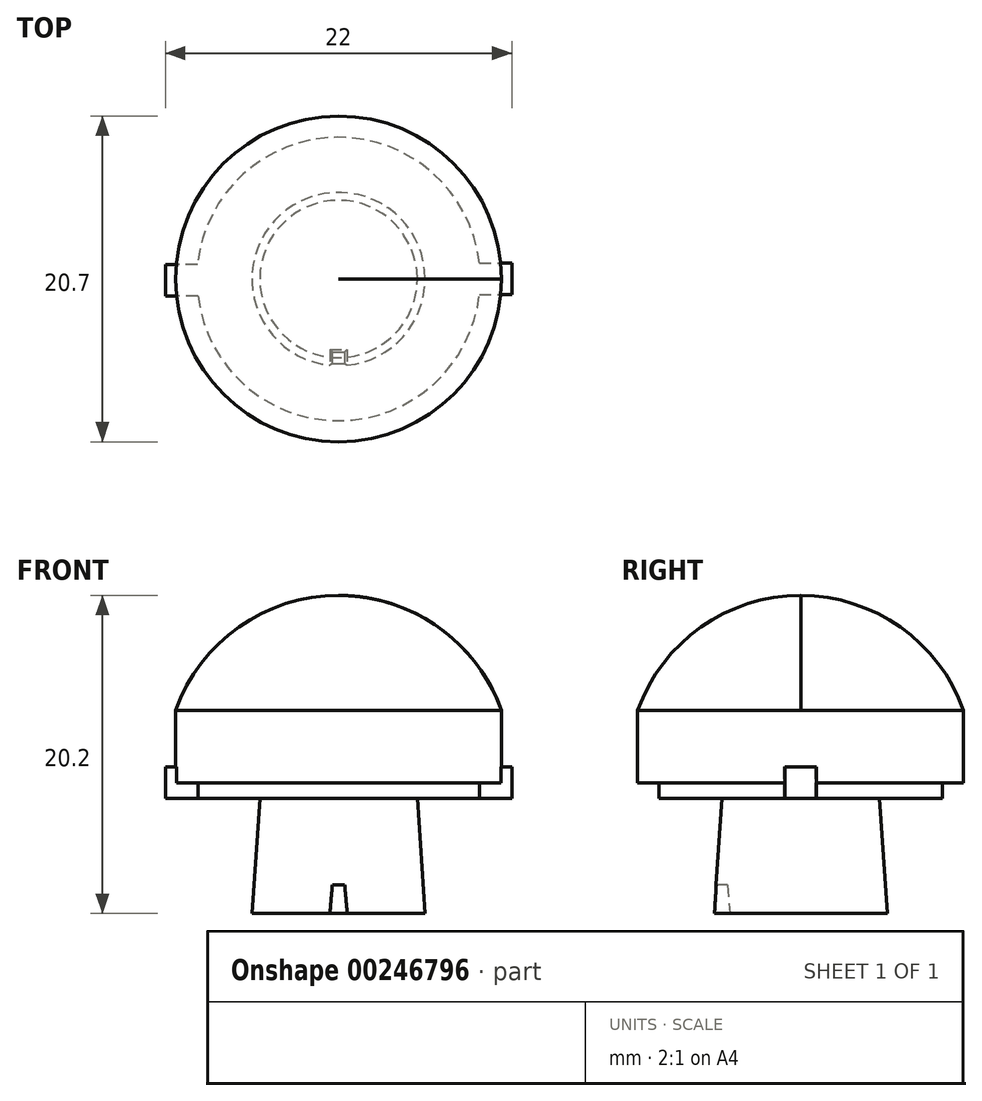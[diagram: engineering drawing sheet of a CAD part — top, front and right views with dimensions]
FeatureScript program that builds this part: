
annotation { "Feature Type Name" : "Feature", "Feature Type Description" : "" }
export const myFeature = defineFeature(function(context is Context, id is Id, definition is map)
    precondition{}
    {
        {
            var Q0;
            Q0=qCreatedBy(makeId("Front.planeOp"),FACE);
            var sketch = newSketch(context, id + "F0", { "sketchPlane" : qUnion([Q0])});
            skLineSegment(sketch, "E0", {"start": v(0, 0) * mm, "end": v(5.5, 0) * mm});
            skLineSegment(sketch, "E1", {"start": v(0, 20.2) * mm, "end": v(16.44, 20.2) * mm, "construction": true});
            skLineSegment(sketch, "E2", {"start": v(10.35, 7.3) * mm, "end": v(10.35, 0) * mm, "construction": true});
            skLineSegment(sketch, "E3", {"start": v(10.35, 7.3) * mm, "end": v(0, 7.3) * mm, "construction": true});
            skLineSegment(sketch, "E4", {"start": v(0, 7.3) * mm, "end": v(5, 7.3) * mm});
            skLineSegment(sketch, "E5", {"start": v(5, 7.3) * mm, "end": v(5.5, 0) * mm});
            skLineSegment(sketch, "E6", {"start": v(5, 7.3) * mm, "end": v(9, 7.3) * mm});
            skLineSegment(sketch, "E7", {"start": v(9, 7.3) * mm, "end": v(9, 8.3) * mm});
            skLineSegment(sketch, "E8", {"start": v(9, 7.3) * mm, "end": v(11, 7.3) * mm, "construction": true});
            skLineSegment(sketch, "E9", {"start": v(11, 7.3) * mm, "end": v(11, 9.3) * mm, "construction": true});
            skLineSegment(sketch, "E10", {"start": v(9, 8.3) * mm, "end": v(10.35, 8.3) * mm});
            skLineSegment(sketch, "E11", {"start": v(10.35, 8.3) * mm, "end": v(10.35, 9.3) * mm});
            skLineSegment(sketch, "E12", {"start": v(10.35, 9.3) * mm, "end": v(11, 9.3) * mm, "construction": true});
            skLineSegment(sketch, "E13", {"start": v(10.35, 9.3) * mm, "end": v(10.35, 12.9) * mm});
            skLineSegment(sketch, "E14", {"start": v(0, 12.9) * mm, "end": v(-10.35, 12.9) * mm, "construction": true});
            skLineSegment(sketch, "E15", {"start": v(0, 12.9) * mm, "end": v(10.35, 12.9) * mm, "construction": true});
            skArc(sketch, "E16", {"start": v(10.35, 12.9) * mm, "mid": v(6.33, 18.2) * mm, "end": v(0, 20.2) * mm});
            skLineSegment(sketch, "E17", {"start": v(0, 0) * mm, "end": v(0, 20.2) * mm});
            skSolve(sketch);
        }
        {
            var Q0;
            Q0=qSketchRegion(id+"F0",true);
            extrude(context, id + "F1", {"entities" : qUnion([Q0]), "depth" : 0.01 * mm});
        }
        {
            var Q0;
            Q0=makeQuery(id+"F1.opExtrude","CAP_FACE",FACE,{"disambiguationData":[OSD([sQuery(id+"F0.wireOp",EDGE,"E0"),sQuery(id+"F0.wireOp",EDGE,"E5"),sQuery(id+"F0.wireOp",EDGE,"E6"),sQuery(id+"F0.wireOp",EDGE,"E7"),sQuery(id+"F0.wireOp",EDGE,"E10"),sQuery(id+"F0.wireOp",EDGE,"E11"),sQuery(id+"F0.wireOp",EDGE,"E13"),sQuery(id+"F0.wireOp",EDGE,"E16"),sQuery(id+"F0.wireOp",EDGE,"74306cc8-111f-4a76-b4a3-b401b2c3296c0.MirrorCS"),sQuery(id+"F0.wireOp",EDGE,"74306cc8-111f-4a76-b4a3-b401b2c3296c2.MirrorCS"),sQuery(id+"F0.wireOp",EDGE,"74306cc8-111f-4a76-b4a3-b401b2c3296c3.MirrorCS"),sQuery(id+"F0.wireOp",EDGE,"74306cc8-111f-4a76-b4a3-b401b2c3296c6.MirrorCS"),sQuery(id+"F0.wireOp",EDGE,"74306cc8-111f-4a76-b4a3-b401b2c3296c7.MirrorCS"),sQuery(id+"F0.wireOp",EDGE,"74306cc8-111f-4a76-b4a3-b401b2c3296c9.MirrorCS"),sQuery(id+"F0.wireOp",EDGE,"74306cc8-111f-4a76-b4a3-b401b2c3296c13.MirrorCS")])],"isStart":false});
            var Q1;
            Q1=makeQuery(id+"F1.opExtrude","CAP_EDGE",EDGE,{"disambiguationData":[OSD([sQuery(id+"F0.wireOp",EDGE,"E17")])],"isStart":false});
            revolve(context, id + "F2", {"operationType" : NewBodyOperationType.ADD, "entities" : qUnion([Q0]), "axis" : qUnion([Q1]), "revolveType" : RevolveType.FULL});
        }
        {
            var Q0;
            {var subQ0=sQuery(id+"F0.wireOp",EDGE,"E0");Q0=makeQuery(id+"F2.boolean.opBoolean","MERGE",FACE,{"derivedFrom":[makeQuery(id+"F1.opExtrude","SWEPT_FACE",FACE,{"disambiguationData":[OSD([subQ0])]}),makeQuery(id+"F2.opRevolve","SWEPT_FACE",FACE,{"disambiguationData":[OSD([subQ0])]})]});}
            var sketch = newSketch(context, id + "F3", { "sketchPlane" : qUnion([Q0])});
            skCircle(sketch, "E18", {"center": v(0, 0) * mm, "radius": 6 * mm, "construction": true});
            skLineSegment(sketch, "E19", {"start": v(0, 6) * mm, "end": v(0, 4.5) * mm, "construction": true});
            skLineSegment(sketch, "E20", {"start": v(0, 4.5) * mm, "end": v(0.55, 4.5) * mm});
            skLineSegment(sketch, "E21", {"start": v(0.55, 4.5) * mm, "end": v(0.55, 5.97) * mm});
            skLineSegment(sketch, "E22", {"start": v(0, 4.5) * mm, "end": v(-0.55, 4.5) * mm});
            skLineSegment(sketch, "E23", {"start": v(-0.55, 4.5) * mm, "end": v(-0.55, 5.97) * mm});
            skLineSegment(sketch, "E24", {"start": v(-0.55, 5.97) * mm, "end": v(0.55, 5.97) * mm});
            skSolve(sketch);
        }
        {
            var Q0;
            Q0=qSketchRegion(id+"F3",true);
            extrude(context, id + "F4", {"entities" : qUnion([Q0]), "operationType" : NewBodyOperationType.REMOVE, "oppositeDirection" : true, "depth" : 1.8 * mm});
        }
        {
            var Q0;
            Q0=makeQuery(id+"F4.boolean.opBoolean","COPY",EDGE,{"derivedFrom":makeQuery(id+"F4.opExtrude","CAP_EDGE",EDGE,{"disambiguationData":[OSD([sQuery(id+"F3.wireOp",EDGE,"E23")])],"isStart":false})});
            var Q1;
            Q1=makeQuery(id+"F4.boolean.opBoolean","COPY",EDGE,{"derivedFrom":makeQuery(id+"F4.opExtrude","CAP_EDGE",EDGE,{"disambiguationData":[OSD([sQuery(id+"F3.wireOp",EDGE,"E21")])],"isStart":false})});
            var Q2;
            Q2=makeQuery(id+"F4.boolean.opBoolean","COPY",EDGE,{"derivedFrom":makeQuery(id+"F4.opExtrude","CAP_EDGE",EDGE,{"disambiguationData":[OSD([sQuery(id+"F3.wireOp",EDGE,"E20"),sQuery(id+"F3.wireOp",EDGE,"E22")])],"isStart":false})});
            chamfer(context, id + "F5", {"entities" : qUnion([Q0, Q1, Q2]), "chamferType" : ChamferType.OFFSET_ANGLE, "width" : 1.8 * mm, "oppositeDirection" : false, "angle" : 5 * degree, "tangentPropagation" : true});
        }
        {
            var Q0;
            Q0=qCreatedBy(makeId("Front.planeOp"),FACE);
            var sketch = newSketch(context, id + "F6", { "sketchPlane" : qUnion([Q0])});
            skLineSegment(sketch, "E25", {"start": v(10.35, 9.3) * mm, "end": v(11, 9.3) * mm});
            skLineSegment(sketch, "E26", {"start": v(11, 9.3) * mm, "end": v(11, 7.3) * mm});
            skLineSegment(sketch, "E27", {"start": v(11, 7.3) * mm, "end": v(9, 7.3) * mm});
            skLineSegment(sketch, "E28", {"start": v(9, 7.3) * mm, "end": v(9, 8.3) * mm});
            skLineSegment(sketch, "E29", {"start": v(9, 8.3) * mm, "end": v(10.35, 8.3) * mm});
            skLineSegment(sketch, "E30", {"start": v(10.35, 8.3) * mm, "end": v(10.35, 9.3) * mm});
            skLineSegment(sketch, "E31.MirrorCS", {"start": v(-10.35, 9.3) * mm, "end": v(-11, 9.3) * mm});
            skLineSegment(sketch, "E32.MirrorCS", {"start": v(-10.35, 8.3) * mm, "end": v(-10.35, 9.3) * mm});
            skLineSegment(sketch, "E33.MirrorCS", {"start": v(-9, 7.3) * mm, "end": v(-9, 8.3) * mm});
            skLineSegment(sketch, "E34.MirrorCS", {"start": v(-11, 7.3) * mm, "end": v(-9, 7.3) * mm});
            skLineSegment(sketch, "E35.MirrorCS", {"start": v(-11, 9.3) * mm, "end": v(-11, 7.3) * mm});
            skLineSegment(sketch, "E36.MirrorCS", {"start": v(-9, 8.3) * mm, "end": v(-10.35, 8.3) * mm});
            skSolve(sketch);
        }
        {
            var Q0;
            Q0=qSketchRegion(id+"F6",true);
            extrude(context, id + "F7", {"entities" : qUnion([Q0]), "operationType" : NewBodyOperationType.ADD, "depth" : 0.1 * mm});
        }
        {
            var Q0;
            Q0=makeQuery(id+"F7.opExtrude","SWEPT_FACE",FACE,{"disambiguationData":[OSD([sQuery(id+"F6.wireOp",EDGE,"E26")])]});
            var sketch = newSketch(context, id + "F8", { "sketchPlane" : qUnion([Q0])});
            skLineSegment(sketch, "E37.bottom", {"start": v(-1, 9.3) * mm, "end": v(0, 9.3) * mm});
            skLineSegment(sketch, "E37.top", {"start": v(-1, 7.3) * mm, "end": v(0, 7.3) * mm});
            skLineSegment(sketch, "E37.left", {"start": v(-1, 9.3) * mm, "end": v(-1, 7.3) * mm});
            skLineSegment(sketch, "E38.MirrorCS", {"start": v(1, 9.3) * mm, "end": v(1, 7.3) * mm});
            skLineSegment(sketch, "E39.MirrorCS", {"start": v(1, 7.3) * mm, "end": v(0, 7.3) * mm});
            skLineSegment(sketch, "E40.MirrorCS", {"start": v(1, 9.3) * mm, "end": v(0, 9.3) * mm});
            skSolve(sketch);
        }
        {
            var Q0;
            Q0=qSketchRegion(id+"F8",true);
            extrude(context, id + "F9", {"entities" : qUnion([Q0]), "operationType" : NewBodyOperationType.ADD, "endBound" : BoundingType.UP_TO_NEXT, "oppositeDirection" : true, "depth" : 25 * mm});
        }
        {
            var Q0;
            Q0=makeQuery(id+"F7.opExtrude","SWEPT_FACE",FACE,{"disambiguationData":[OSD([sQuery(id+"F6.wireOp",EDGE,"E35.MirrorCS")])]});
            var sketch = newSketch(context, id + "F10", { "sketchPlane" : qUnion([Q0])});
            skLineSegment(sketch, "E41.bottom", {"start": v(0.1, 9.3) * mm, "end": v(-0.9, 9.3) * mm});
            skLineSegment(sketch, "E41.right", {"start": v(-0.9, 9.3) * mm, "end": v(-0.9, 7.3) * mm});
            skLineSegment(sketch, "E42", {"start": v(-0.9, 7.3) * mm, "end": v(0.1, 7.3) * mm});
            skLineSegment(sketch, "E43", {"start": v(1.1, 7.3) * mm, "end": v(0.1, 7.3) * mm});
            skLineSegment(sketch, "E44", {"start": v(0.1, 9.3) * mm, "end": v(1.1, 9.3) * mm});
            skLineSegment(sketch, "E45", {"start": v(1.1, 9.3) * mm, "end": v(1.1, 7.3) * mm});
            skSolve(sketch);
        }
        {
            var Q0;
            Q0=qSketchRegion(id+"F10",true);
            extrude(context, id + "F11", {"entities" : qUnion([Q0]), "operationType" : NewBodyOperationType.ADD, "endBound" : BoundingType.UP_TO_NEXT, "oppositeDirection" : true, "depth" : 25 * mm});
        }
    });
